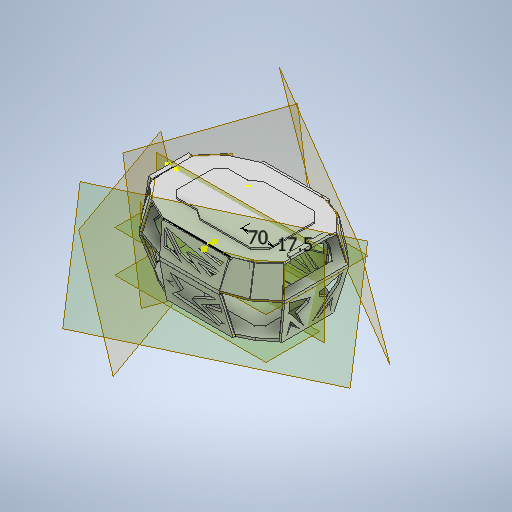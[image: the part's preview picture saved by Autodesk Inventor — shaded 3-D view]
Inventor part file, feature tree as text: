
AUTODESK INVENTOR PART (.ipt)
format: ipt  version: 2025.2 (Build 292293000, 293)  size: 6,002,176 bytes
history: native  units: mm
features: sketch x40, extrude x31, other x23, plane x17, loft x11, mirror x2
ambient origin geometry x8: Origin, YZ Plane, XZ Plane, XY Plane, X Axis, Y Axis, Z Axis, Center Point
bodies: Body1 (feature_tree)
feature tree (124):
  extrude  "Extrusion2"  Depth=45.0mm
  extrude  "Extrusion3"  Depth=40.0mm
  plane  "Work Plane3"
  extrude  "Extrusion4"  Depth=145.0mm
  extrude  "Extrusion5"  Depth=55.0mm
  plane  "Work Plane4"
  extrude  "Extrusion6"  Depth=40.0mm
  sketch  "Sketch8"  dims[d17=165.0deg d18=15.0mm]
  sketch  "Sketch9"  dims[d20=10.0mm d21=40.0mm]
  sketch  "Sketch10"  dims[d22=5.0mm d23=5.0mm]
  loft  "Loft1"
  loft  "Loft2"
  extrude  "Extrusion7"  Depth=5.0mm
  extrude  "Extrusion8"  TaperAngle=90.0deg  [1 undecoded]
  extrude  "Extrusion9"  Depth=30.0mm
  sketch  "Sketch14"  dims[d30=45.0mm d31=20.0mm]
  sketch  "Sketch15"  dims[d32=45.0deg d39=5.0mm d40=0.0mm]
  sketch  "Sketch16"  dims[d41=3.0mm d42=3.0mm d43=0.0mm d44=0.0mm d45=150.0mm]
  loft  "Loft3"
  loft  "Loft4"
  loft  "Loft5"
  extrude  "Extrusion10"  Depth=3.0mm
  extrude  "Extrusion11"  Depth=10.0mm
  extrude  "Extrusion12"  Depth=10.0mm
  extrude  "Extrusion13"  Depth=10.0mm
  extrude  "Extrusion14"  Depth=10.0mm
  loft  "Loft7"
  loft  "Loft8"
  sketch  "Sketch22"  dims[d57=10.0mm d58=10.0mm]
  plane  "Work Plane5"
  extrude  "Extrusion15"  Depth=3.0mm TaperAngle=0.0deg
  plane  "Work Plane6"
  extrude  "Extrusion16"  Depth=10.0mm
  extrude  "Extrusion17"  Depth=50.0mm
  plane  "Work Plane7"
  extrude  "Extrusion18"  Depth=50.0mm
  sketch  "Sketch28"  dims[d71=27.925268mm d72=10.0mm]
  extrude  "Extrusion19"  Depth=10.0mm
  extrude  "Extrusion20"  Depth=60.0mm
  extrude  "Extrusion21"  Depth=5.0mm TaperAngle=0.0deg
  extrude  "Extrusion22"  TaperAngle=0.0deg  [1 undecoded]
  extrude  "Extrusion23"  TaperAngle=0.0deg  [1 undecoded]
  extrude  "Extrusion24"  Depth=4.0mm TaperAngle=0.0deg
  extrude  "Extrusion25"  TaperAngle=0.0deg  [1 undecoded]
  extrude  "Extrusion26"  TaperAngle=0.0deg  [1 undecoded]
  extrude  "Extrusion27"  TaperAngle=0.0deg  [1 undecoded]
  plane  "Work Plane8"
  mirror  "Mirror1"
  loft  "Loft9"
  loft  "Loft10"
  loft  "Loft11"
  loft  "Loft12"
  plane  "Work Plane14"
  plane  "Work Plane15"
  extrude  "Extrusion28"  TaperAngle=0.0deg  [1 undecoded]
  extrude  "Extrusion29"  Depth=4.0mm TaperAngle=0.0deg
  plane  "Work Plane16"
  extrude  "Extrusion30"  Depth=5.0mm
  mirror  "Mirror2"
  extrude  "Extrusion31"  Depth=5.0mm TaperAngle=0.0deg
  sketch  "Sketch42"  dims[d126=4.0mm d127=0.0mm d128=4.0mm d129=0.0mm]
  extrude  "Extrusion32"  Depth=5.0mm
  sketch  "Sketch1"  dims[d6=115.0mm d8=45.0mm]
  other  "Image1"
  sketch  "Sketch3"  dims[d9=45.0deg d10=40.0mm]
  sketch  "Sketch4"  dims[d11=27.925268mm d12=145.0mm]
  sketch  "Sketch5"  dims[d13=27.052603mm d14=55.0mm]
  sketch  "Sketch6"  dims[d15=27.052603mm d16=40.0mm]
  other  "Edges1"
  other  "Edges2"
  other  "Edges3"
  other  "Edges4"
  sketch  "Sketch11"  dims[d24=40.0mm d25=90.0deg]
  sketch  "Sketch12"  dims[d26=30.0mm d27=110.0mm]
  sketch  "Sketch13"  dims[d28=25.0mm d29=25.307274mm]
  other  "Edges5"
  other  "Edges6"
  other  "Edges7"
  other  "Edges8"
  other  "Edges9"
  other  "Edges10"
  sketch  "Sketch17"  dims[d46=10.0mm d48=10.0mm]
  sketch  "Sketch18"  dims[d49=10.0mm d50=22.68928mm]
  sketch  "Sketch19"  dims[d51=10.0mm d52=10.0mm]
  sketch  "Sketch20"  dims[d53=10.0mm d54=10.0mm]
  sketch  "Sketch21"  dims[d55=10.0mm d56=10.0mm]
  other  "Edges13"
  other  "Edges14"
  other  "Edges15"
  other  "Edges16"
  sketch  "Sketch23"  dims[d59=5.0mm d60=0.0mm d61=3.0mm d62=3.0mm d63=0.0mm d64=0.0mm]
  sketch  "Sketch24"  dims[d65=-90.0mm d66=10.0mm]
  sketch  "Sketch25"  dims[d67=70.0mm d68=50.0mm]
  sketch  "Sketch26"  dims[d69=22.68928mm d70=50.0mm]
  sketch  "Sketch29"  dims[d73=50.0mm d74=60.0mm]
  sketch  "Sketch30"  dims[d75=70.0mm d76=5.0mm d77=0.0mm]
  sketch  "Sketch31"  dims[d78=0.0mm d79=90.0deg d80=0.0mm d81=90.0deg]
  sketch  "Sketch32"  dims[d82=0.0mm d83=90.0deg d84=0.0mm d85=90.0deg]
  sketch  "Sketch33"  dims[d86=4.0mm d87=0.0mm d88=4.0mm d89=0.0mm]
  sketch  "Sketch34"  dims[d90=4.0mm d91=0.0mm d92=0.0mm d93=90.0deg]
  sketch  "Sketch35"  dims[d94=0.0mm d95=90.0deg d96=0.0mm d97=90.0deg]
  sketch  "Sketch36"  dims[d98=0.0mm d99=90.0deg d100=0.0mm d101=90.0deg]
  sketch  "Sketch37"  dims[d102=0.0mm d103=90.0deg d104=4.0mm d105=0.0mm]
  plane  "Work Plane9"
  plane  "Work Plane10"
  plane  "Work Plane11"
  plane  "Work Plane12"
  plane  "Work Plane13"
  other  "Edges17"
  other  "Edges18"
  other  "Edges19"
  other  "Edges20"
  other  "Edges21"
  other  "Edges22"
  other  "Edges23"
  other  "Edges24"
  sketch  "Sketch38"  dims[d106=4.0mm d107=0.0mm d108=4.0mm d109=0.0mm]
  sketch  "Sketch39"  dims[d110=4.0mm d111=0.0mm d112=4.0mm d113=0.0mm]
  sketch  "Sketch40"  dims[d118=0.0mm d119=90.0deg d120=0.0mm d121=90.0deg]
  plane  "Work Plane17"
  plane  "Work Plane18"
  plane  "Work Plane19"
  sketch  "Sketch41"  dims[d122=0.0mm d123=90.0deg d124=0.0mm d125=90.0deg]
  sketch  "Sketch43"  dims[d130=4.0mm d131=0.0mm d132=92.689mm d133=4.0mm d134=0.0mm d135=70.0mm d136=17.5mm d137=5.0mm d138=25.0mm d139=70.0mm d140=25.0mm d141=17.5mm d142=90.0deg d143=23.0mm d144=0.0mm d145=70.0mm d146=3.0mm d147=17.5mm d148=0.0mm d149=25.0mm d150=30.0mm d151=15.0deg d152=90.0deg d153=5.0mm d154=20.0mm d155=90.0deg d156=4.363323mm d157=17.5mm d158=0.0mm d159=25.0mm d160=165.0deg d161=40.0mm d162=150.0deg d163=50.0mm d164=1.745329mm d165=40.0mm d166=5.0mm d167=40.0mm d168=30.543262mm d169=17.5mm d170=0.0mm d171=10.0mm d172=100.0mm d173=150.0deg d174=40.0mm d175=19.198622mm d176=100.0mm d177=70.0mm d178=30.0deg d179=100.0mm d180=10.0mm d181=10.0mm d182=10.0mm d183=4.363323mm d184=40.0mm d185=40.0mm d186=6.981317mm d187=20.0mm d188=24.43461mm d189=16.0mm d190=10.0mm d191=0.0mm d192=80.0mm d193=24.43461mm d194=120.0mm d195=30.0deg d196=40.0mm d197=30.0deg d198=50.0mm d199=10.0mm d200=50.0mm d201=55.0mm d202=1.745329mm d203=30.0mm d204=27.925268mm d205=40.0mm d206=5.0mm d207=30.0mm d208=30.0mm d209=17.453293mm d210=60.0mm d211=30.0mm d212=50.0mm d213=0.0mm d214=10.0mm d215=10.0mm d216=10.0mm d217=10.0mm d218=90.0deg d219=10.0mm d220=20.0mm d221=10.0mm d222=17.453293mm d223=25.0mm d224=22.68928mm d225=70.0mm d226=10.0mm d227=40.0mm d228=22.68928mm d229=20.0mm d230=75.0deg d231=50.0mm d232=0.0mm d233=5.0mm d234=0.0mm d235=5.0mm d236=0.0mm d238=0.0mm d239=90.0deg d240=0.0mm d241=90.0deg d242=0.0mm d243=90.0deg d244=0.0mm d245=90.0deg d246=0.0mm d247=90.0deg d248=0.0mm d249=90.0deg d250=0.0mm d251=90.0deg d252=0.0mm d253=90.0deg d254=3.0mm d255=0.0mm d256=3.0mm d257=0.0mm d258=3.0mm d259=0.0mm d260=30.0mm d261=50.0mm d262=90.0mm d263=30.0mm d264=5.0mm d265=0.0mm d266=20.0mm d267=100.0mm d268=20.0mm d269=100.0mm d270=30.0mm d271=40.0mm d272=30.0mm d273=5.0mm d274=5.0mm d275=0.0mm d276=0.0mm]
note: 7 required parameter values undecoded (feature->parameter linkage not recoverable at this tier; creation-order binding heuristic only, values carry confidence <= 0.55)
